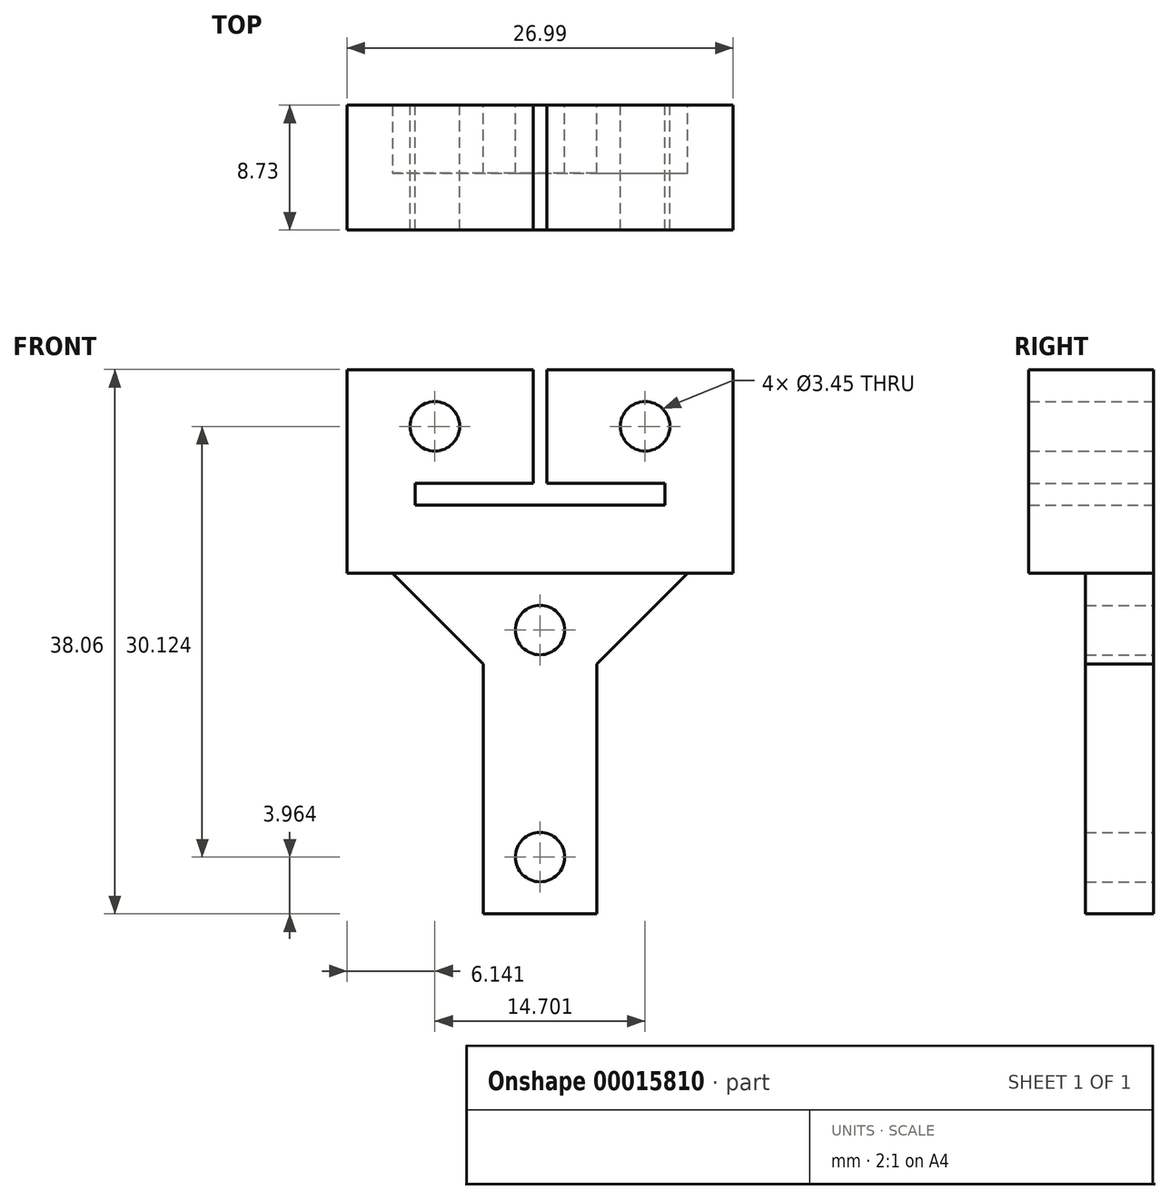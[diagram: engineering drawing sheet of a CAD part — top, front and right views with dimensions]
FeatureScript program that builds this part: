
annotation { "Feature Type Name" : "Feature", "Feature Type Description" : "" }
export const myFeature = defineFeature(function(context is Context, id is Id, definition is map)
    precondition{}
    {
        {
            var Q0;
            Q0=qCreatedBy(makeId("Front.planeOp"),FACE);
            var sketch = newSketch(context, id + "F0", { "sketchPlane" : qUnion([Q0])});
            skLineSegment(sketch, "E0", {"start": v(0, 0) * mm, "end": v(17.46, 0) * mm});
            skLineSegment(sketch, "E1.top", {"start": v(8.26, 9.49) * mm, "end": v(-4.76, 9.49) * mm});
            skLineSegment(sketch, "E1.right", {"start": v(-4.76, -4.76) * mm, "end": v(-4.76, 9.49) * mm});
            skLineSegment(sketch, "E2.top", {"start": v(9.2, 9.49) * mm, "end": v(22.23, 9.49) * mm});
            skLineSegment(sketch, "E2.right", {"start": v(22.23, -4.76) * mm, "end": v(22.23, 9.49) * mm});
            skLineSegment(sketch, "E3", {"start": v(-4.76, -4.76) * mm, "end": v(4.76, -4.76) * mm});
            skLineSegment(sketch, "E4", {"start": v(22.23, -4.76) * mm, "end": v(12.7, -4.76) * mm});
            skLineSegment(sketch, "E5.bottom", {"start": v(12.7, -4.76) * mm, "end": v(4.76, -4.76) * mm, "construction": true});
            skLineSegment(sketch, "E5.top", {"start": v(12.7, -28.58) * mm, "end": v(4.76, -28.58) * mm});
            skLineSegment(sketch, "E5.left", {"start": v(12.7, -4.76) * mm, "end": v(12.7, -28.58) * mm});
            skLineSegment(sketch, "E5.right", {"start": v(4.76, -4.76) * mm, "end": v(4.76, -28.58) * mm});
            skLineSegment(sketch, "E6", {"start": v(0, 0) * mm, "end": v(0, 1.55) * mm});
            skLineSegment(sketch, "E7", {"start": v(17.46, 0) * mm, "end": v(17.46, 1.55) * mm});
            skLineSegment(sketch, "E8.bottom", {"start": v(0, 1.55) * mm, "end": v(8.26, 1.55) * mm});
            skLineSegment(sketch, "E8.right", {"start": v(8.26, 1.55) * mm, "end": v(8.26, 9.49) * mm});
            skLineSegment(sketch, "E9.bottom", {"start": v(17.46, 1.55) * mm, "end": v(9.2, 1.55) * mm});
            skLineSegment(sketch, "E9.right", {"start": v(9.2, 1.55) * mm, "end": v(9.2, 9.49) * mm});
            skLineSegment(sketch, "E10", {"start": v(9.2, 9.49) * mm, "end": v(8.26, 9.49) * mm, "construction": true});
            skLineSegment(sketch, "E11", {"start": v(17.46, 0) * mm, "end": v(17.46, -4.76) * mm});
            skLineSegment(sketch, "E12", {"start": v(17.46, 0) * mm, "end": v(22.23, 0) * mm});
            skLineSegment(sketch, "E13", {"start": v(8.73, -4.76) * mm, "end": v(8.73, -8.73) * mm});
            skLineSegment(sketch, "E14", {"start": v(8.73, -28.58) * mm, "end": v(8.73, -24.6) * mm});
            skCircle(sketch, "E15", {"center": v(8.73, -8.73) * mm, "radius": 1.73 * mm});
            skCircle(sketch, "E16", {"center": v(8.73, -24.6) * mm, "radius": 1.73 * mm});
            skLineSegment(sketch, "E17", {"start": v(9.2, 5.52) * mm, "end": v(16.08, 5.52) * mm});
            skLineSegment(sketch, "E18", {"start": v(8.26, 5.52) * mm, "end": v(1.38, 5.52) * mm});
            skCircle(sketch, "E19", {"center": v(16.08, 5.52) * mm, "radius": 1.73 * mm});
            skCircle(sketch, "E20", {"center": v(1.38, 5.52) * mm, "radius": 1.73 * mm});
            skSolve(sketch);
        }
        {
            var Q0;
            Q0=qSketchRegion(id+"F0",true);
            extrude(context, id + "F1", {"entities" : qUnion([Q0]), "depth" : 4.76 * mm});
        }
        {
            var Q0;
            Q0=makeQuery(id+"F1.opExtrude","CAP_FACE",FACE,{"disambiguationData":[OSD([sQuery(id+"F0.wireOp",EDGE,"E0"),sQuery(id+"F0.wireOp",EDGE,"E1.top"),sQuery(id+"F0.wireOp",EDGE,"E1.right"),sQuery(id+"F0.wireOp",EDGE,"E2.top"),sQuery(id+"F0.wireOp",EDGE,"E2.right"),sQuery(id+"F0.wireOp",EDGE,"E3"),sQuery(id+"F0.wireOp",EDGE,"E4"),sQuery(id+"F0.wireOp",EDGE,"E5.top"),sQuery(id+"F0.wireOp",EDGE,"E5.left"),sQuery(id+"F0.wireOp",EDGE,"E5.right"),sQuery(id+"F0.wireOp",EDGE,"E6"),sQuery(id+"F0.wireOp",EDGE,"E7"),sQuery(id+"F0.wireOp",EDGE,"E8.bottom"),sQuery(id+"F0.wireOp",EDGE,"E8.right"),sQuery(id+"F0.wireOp",EDGE,"E9.bottom"),sQuery(id+"F0.wireOp",EDGE,"E9.right"),sQuery(id+"F0.wireOp",EDGE,"E15"),sQuery(id+"F0.wireOp",EDGE,"E16"),sQuery(id+"F0.wireOp",EDGE,"E19"),sQuery(id+"F0.wireOp",EDGE,"E20")])],"isStart":false});
            var sketch = newSketch(context, id + "F2", { "sketchPlane" : qUnion([Q0])});
            skLineSegment(sketch, "E21.top", {"start": v(-4.76, -4.76) * mm, "end": v(22.23, -4.76) * mm});
            skLineSegment(sketch, "E21.left", {"start": v(-4.76, 9.49) * mm, "end": v(-4.76, -4.76) * mm});
            skLineSegment(sketch, "E21.right", {"start": v(22.23, 9.49) * mm, "end": v(22.23, -4.76) * mm});
            skLineSegment(sketch, "E22", {"start": v(-4.76, 9.49) * mm, "end": v(8.26, 9.49) * mm});
            skLineSegment(sketch, "E23", {"start": v(8.26, 9.49) * mm, "end": v(8.26, 1.55) * mm});
            skLineSegment(sketch, "E24", {"start": v(8.26, 1.55) * mm, "end": v(0, 1.55) * mm});
            skLineSegment(sketch, "E25", {"start": v(0, 1.55) * mm, "end": v(0, 0) * mm});
            skLineSegment(sketch, "E26", {"start": v(0, 0) * mm, "end": v(17.46, 0) * mm});
            skLineSegment(sketch, "E27", {"start": v(17.46, 0) * mm, "end": v(17.46, 1.55) * mm});
            skLineSegment(sketch, "E28", {"start": v(17.46, 1.55) * mm, "end": v(9.2, 1.55) * mm});
            skLineSegment(sketch, "E29", {"start": v(9.2, 1.55) * mm, "end": v(9.2, 9.49) * mm});
            skLineSegment(sketch, "E30", {"start": v(9.2, 9.49) * mm, "end": v(22.23, 9.49) * mm});
            skCircle(sketch, "E31", {"center": v(1.38, 5.52) * mm, "radius": 1.73 * mm});
            skCircle(sketch, "E32", {"center": v(16.08, 5.52) * mm, "radius": 1.73 * mm});
            skSolve(sketch);
        }
        {
            var Q0;
            Q0=qSketchRegion(id+"F2",true);
            extrude(context, id + "F3", {"entities" : qUnion([Q0]), "operationType" : NewBodyOperationType.ADD, "depth" : 3.97 * mm});
        }
        {
            var Q0;
            Q0=makeQuery(id+"F1.opExtrude","SWEPT_EDGE",EDGE,{"disambiguationData":[OSD([sQuery(id+"F0.wireOp",EDGE,"E3"),sQuery(id+"F0.wireOp",EDGE,"E5.right")])]});
            var Q1;
            Q1=makeQuery(id+"F1.opExtrude","SWEPT_EDGE",EDGE,{"disambiguationData":[OSD([sQuery(id+"F0.wireOp",EDGE,"E4"),sQuery(id+"F0.wireOp",EDGE,"E5.left")])]});
            chamfer(context, id + "F4", {"entities" : qUnion([Q0, Q1]), "width" : 6.35 * mm, "tangentPropagation" : true});
        }
    });
